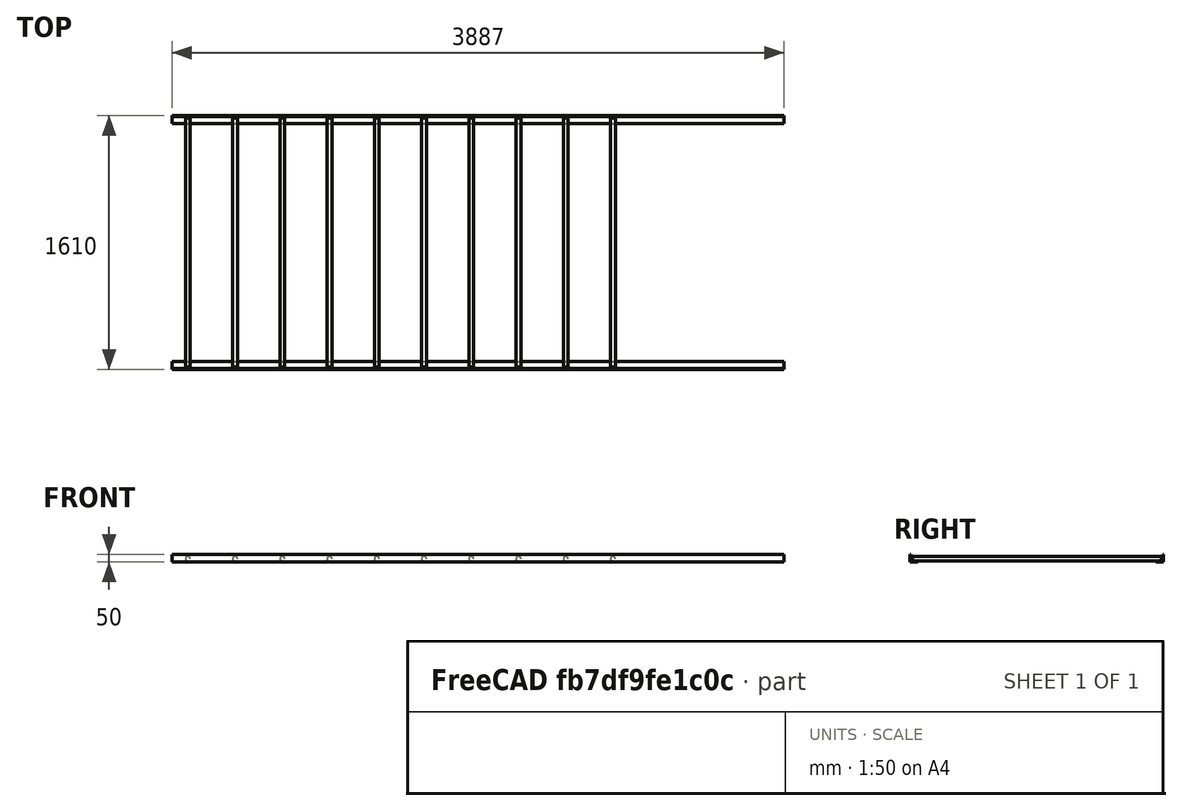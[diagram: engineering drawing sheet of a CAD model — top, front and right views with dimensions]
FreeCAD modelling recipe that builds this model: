
FCSTD DOCUMENT  (FreeCAD 0.18R16131 (Git))
Label: hrazda3
License: All rights reserved
LicenseURL: http://en.wikipedia.org/wiki/All_rights_reserved
objects: Part::Box×4, Part::Cut×2, Part::Cylinder×1, Part::FeaturePython×1
note: 8 computed .brp shape members not serialized (recipe doc carries the construction recipe); baked Part::Feature solids carry a one-line shape summary decoded from their .brp

FEATURE [Part::Box] Box
  AttacherType = Attacher::AttachEngine3D
  Height = 50
  Length = 3887
  Width = 50
FEATURE [Part::Box] Box001
  AttacherType = Attacher::AttachEngine3D
  Height = 50
  Length = 3887
  Placement = pos=(0,5,5) rot=(0,0,1;0rad)
  Width = 50
FEATURE [Part::Cut] Cut
  Base = -> Box
  Tool = -> Box001
FEATURE [Part::Box] Box002
  AttacherType = Attacher::AttachEngine3D
  Height = 50
  Length = 3887
  Placement = pos=(0,1560,0) rot=(0,0,1;0rad)
  Width = 50
FEATURE [Part::Box] Box003
  AttacherType = Attacher::AttachEngine3D
  Height = 50
  Length = 3887
  Placement = pos=(0,1555,5) rot=(0,0,1;0rad)
  Width = 50
FEATURE [Part::Cut] Cut001
  Base = -> Box002
  Tool = -> Box003
FEATURE [Part::Cylinder] Cylinder001
  Angle = 360
  AttacherType = Attacher::AttachEngine3D
  Height = 1580
  Placement = pos=(100,15,21) rot=(1,0,0;-1.5708rad)
  Radius = 15
FEATURE [Part::FeaturePython] Array  # Draft array (typed FeaturePython)
  Angle = 360
  ArrayType = 0
  Axis = (0,0,1)
  Base = -> Cylinder001
  Center = (0,0,0)
  Fuse = false
  IntervalAxis = (0,0,0)
  IntervalX = (300,0,0)
  IntervalY = (0,1,0)
  IntervalZ = (0,0,1)
  NumberPolar = 1
  NumberX = 10
  NumberY = 1
  NumberZ = 1
